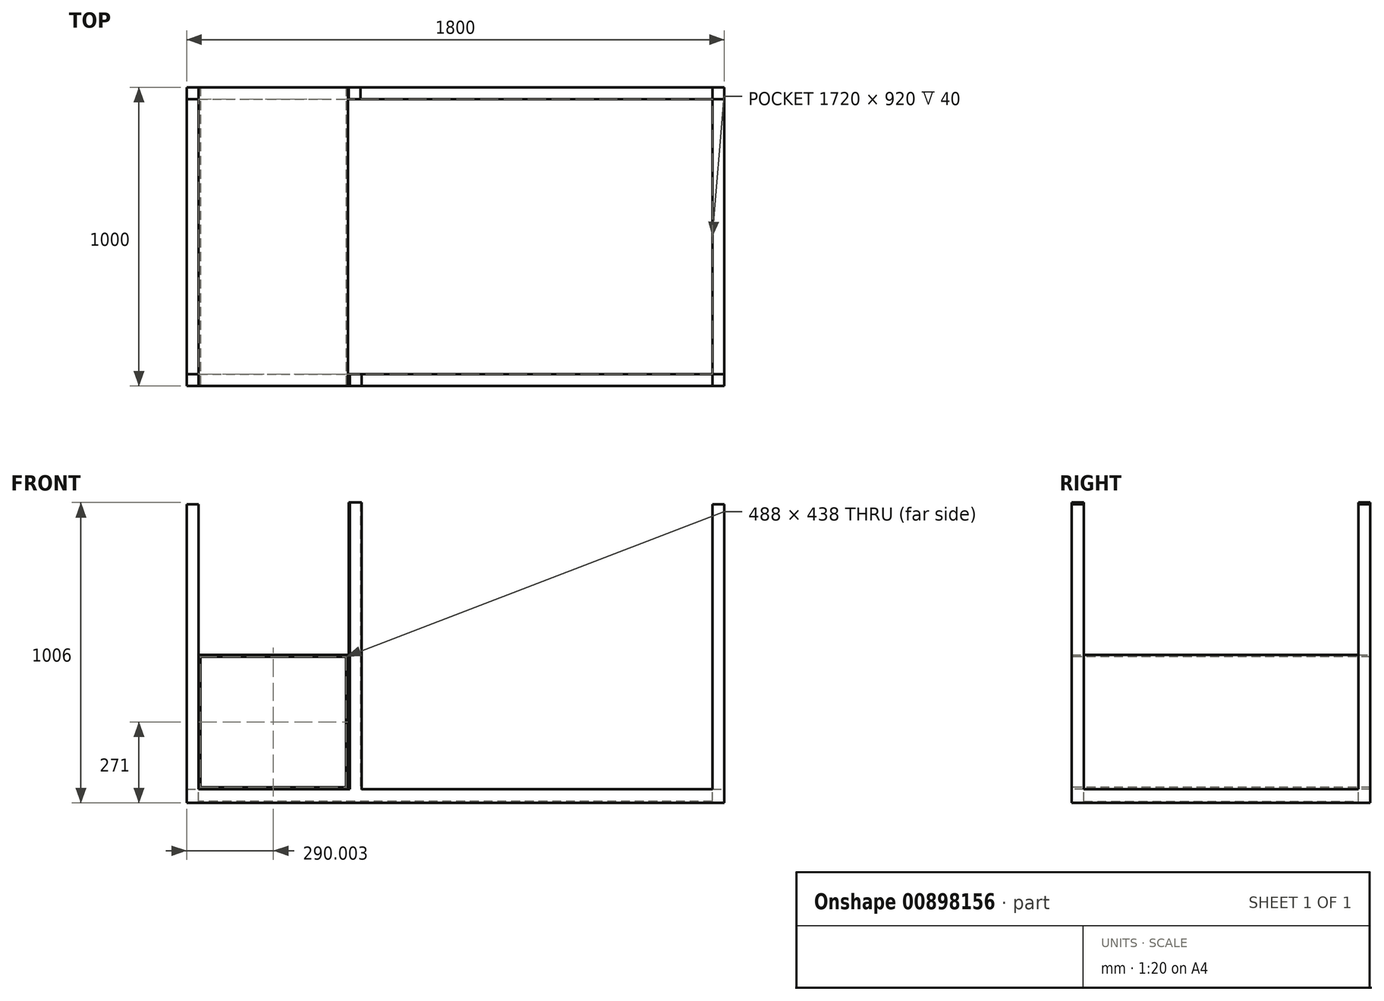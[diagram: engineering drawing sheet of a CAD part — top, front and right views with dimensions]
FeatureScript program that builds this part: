
annotation { "Feature Type Name" : "Feature", "Feature Type Description" : "" }
export const myFeature = defineFeature(function(context is Context, id is Id, definition is map)
    precondition{}
    {
        {
            var Q0;
            Q0=qCreatedBy(makeId("Top.planeOp"),FACE);
            var sketch = newSketch(context, id + "F0", { "sketchPlane" : qUnion([Q0])});
            skLineSegment(sketch, "E0.bottom", {"start": v(-904.96, 573.3) * mm, "end": v(895.04, 573.3) * mm});
            skLineSegment(sketch, "E0.top", {"start": v(-904.96, -426.7) * mm, "end": v(895.04, -426.7) * mm});
            skLineSegment(sketch, "E0.left", {"start": v(-904.96, 573.3) * mm, "end": v(-904.96, -426.7) * mm});
            skLineSegment(sketch, "E0.right", {"start": v(895.04, 573.3) * mm, "end": v(895.04, -426.7) * mm});
            skSolve(sketch);
        }
        {
            var Q0;
            Q0=makeQuery(id+"F0.imprint","IMPRINT",FACE,{"disambiguationData":[TD([[makeQuery(id+"F0.imprint","IMPRINT",EDGE,{"derivedFrom":sQuery(id+"F0.wireOp",EDGE,"E0.bottom")}),-1.0]])]});
            extrude(context, id + "F1", {"entities" : qUnion([Q0]), "depth" : 6 * mm, "offsetDistance" : 25 * mm});
        }
        {
            var Q0;
            Q0=makeQuery(id+"F1.opExtrude","CAP_FACE",FACE,{"disambiguationData":[OSD([sQuery(id+"F0.wireOp",EDGE,"E0.bottom"),sQuery(id+"F0.wireOp",EDGE,"E0.top"),sQuery(id+"F0.wireOp",EDGE,"E0.left"),sQuery(id+"F0.wireOp",EDGE,"E0.right")])],"isStart":true});
            var sketch = newSketch(context, id + "F2", { "sketchPlane" : qUnion([Q0])});
            skLineSegment(sketch, "E1.bottom", {"start": v(-904.96, -573.3) * mm, "end": v(-864.96, -573.3) * mm});
            skLineSegment(sketch, "E1.top", {"start": v(-904.96, -533.3) * mm, "end": v(-864.96, -533.3) * mm});
            skLineSegment(sketch, "E1.left", {"start": v(-904.96, -573.3) * mm, "end": v(-904.96, -533.3) * mm});
            skLineSegment(sketch, "E1.right", {"start": v(-864.96, -573.3) * mm, "end": v(-864.96, -533.3) * mm});
            skLineSegment(sketch, "E2.bottom", {"start": v(895.04, -573.3) * mm, "end": v(855.04, -573.3) * mm});
            skLineSegment(sketch, "E2.top", {"start": v(895.04, -533.3) * mm, "end": v(855.04, -533.3) * mm});
            skLineSegment(sketch, "E2.left", {"start": v(895.04, -573.3) * mm, "end": v(895.04, -533.3) * mm});
            skLineSegment(sketch, "E2.right", {"start": v(855.04, -573.3) * mm, "end": v(855.04, -533.3) * mm});
            skLineSegment(sketch, "E3.bottom", {"start": v(895.04, 426.7) * mm, "end": v(855.04, 426.7) * mm});
            skLineSegment(sketch, "E3.top", {"start": v(895.04, 386.7) * mm, "end": v(855.04, 386.7) * mm});
            skLineSegment(sketch, "E3.left", {"start": v(895.04, 426.7) * mm, "end": v(895.04, 386.7) * mm});
            skLineSegment(sketch, "E3.right", {"start": v(855.04, 426.7) * mm, "end": v(855.04, 386.7) * mm});
            skLineSegment(sketch, "E4.bottom", {"start": v(-904.96, 426.7) * mm, "end": v(-864.96, 426.7) * mm});
            skLineSegment(sketch, "E4.top", {"start": v(-904.96, 386.7) * mm, "end": v(-864.96, 386.7) * mm});
            skLineSegment(sketch, "E4.left", {"start": v(-904.96, 426.7) * mm, "end": v(-904.96, 386.7) * mm});
            skLineSegment(sketch, "E4.right", {"start": v(-864.96, 426.7) * mm, "end": v(-864.96, 386.7) * mm});
            skSolve(sketch);
        }
        {
            var Q0;
            Q0=makeQuery(id+"F2.imprint","IMPRINT",FACE,{"disambiguationData":[TD([[makeQuery(id+"F2.imprint","IMPRINT",EDGE,{"derivedFrom":sQuery(id+"F2.wireOp",EDGE,"E4.bottom")}),-1.0]])]});
            var Q1;
            Q1=makeQuery(id+"F2.imprint","IMPRINT",FACE,{"disambiguationData":[TD([[makeQuery(id+"F2.imprint","IMPRINT",EDGE,{"derivedFrom":sQuery(id+"F2.wireOp",EDGE,"E3.bottom")}),-1.0]])]});
            var Q2;
            Q2=makeQuery(id+"F2.imprint","IMPRINT",FACE,{"disambiguationData":[TD([[makeQuery(id+"F2.imprint","IMPRINT",EDGE,{"derivedFrom":sQuery(id+"F2.wireOp",EDGE,"E2.bottom")}),1.0]])]});
            var Q3;
            Q3=makeQuery(id+"F2.imprint","IMPRINT",FACE,{"disambiguationData":[TD([[makeQuery(id+"F2.imprint","IMPRINT",EDGE,{"derivedFrom":sQuery(id+"F2.wireOp",EDGE,"E1.bottom")}),1.0]])]});
            extrude(context, id + "F3", {"entities" : qUnion([Q0, Q1, Q2, Q3]), "operationType" : NewBodyOperationType.ADD, "depth" : -1000 * mm, "offsetDistance" : 25 * mm});
        }
        {
            var Q0;
            Q0=makeQuery(id+"F3.opExtrude","SWEPT_FACE",FACE,{"disambiguationData":[OSD([sQuery(id+"F2.wireOp",EDGE,"E3.top")])]});
            var sketch = newSketch(context, id + "F4", { "sketchPlane" : qUnion([Q0])});
            skLineSegment(sketch, "E5.bottom", {"start": v(-855.04, 6) * mm, "end": v(-895.04, 6) * mm});
            skLineSegment(sketch, "E5.top", {"start": v(-855.04, 46) * mm, "end": v(-895.04, 46) * mm});
            skLineSegment(sketch, "E5.left", {"start": v(-855.04, 6) * mm, "end": v(-855.04, 46) * mm});
            skLineSegment(sketch, "E5.right", {"start": v(-895.04, 6) * mm, "end": v(-895.04, 46) * mm});
            skSolve(sketch);
        }
        {
            var Q0;
            Q0=makeQuery(id+"F4.imprint","IMPRINT",FACE,{"disambiguationData":[TD([[makeQuery(id+"F4.imprint","IMPRINT",EDGE,{"derivedFrom":sQuery(id+"F4.wireOp",EDGE,"E5.bottom")}),-1.0]])]});
            extrude(context, id + "F5", {"entities" : qUnion([Q0]), "operationType" : NewBodyOperationType.ADD, "depth" : 935 * mm, "offsetDistance" : 25 * mm});
        }
        {
            var Q0;
            Q0=makeQuery(id+"F5.boolean.opBoolean","MERGE",FACE,{"derivedFrom":[makeQuery(id+"F3.opExtrude","SWEPT_FACE",FACE,{"disambiguationData":[OSD([sQuery(id+"F2.wireOp",EDGE,"E2.right")])]}),makeQuery(id+"F3.opExtrude","SWEPT_FACE",FACE,{"disambiguationData":[OSD([sQuery(id+"F2.wireOp",EDGE,"E3.right")])]}),makeQuery(id+"F5.opExtrude","SWEPT_FACE",FACE,{"disambiguationData":[OSD([sQuery(id+"F4.wireOp",EDGE,"E5.left")])]})]});
            var sketch = newSketch(context, id + "F6", { "sketchPlane" : qUnion([Q0])});
            skLineSegment(sketch, "E6.bottom", {"start": v(-573.3, 6) * mm, "end": v(-533.3, 6) * mm});
            skLineSegment(sketch, "E6.top", {"start": v(-573.3, 46) * mm, "end": v(-533.3, 46) * mm});
            skLineSegment(sketch, "E6.left", {"start": v(-573.3, 6) * mm, "end": v(-573.3, 46) * mm});
            skLineSegment(sketch, "E6.right", {"start": v(-533.3, 6) * mm, "end": v(-533.3, 46) * mm});
            skSolve(sketch);
        }
        {
            var Q0;
            Q0=makeQuery(id+"F6.imprint","IMPRINT",FACE,{"disambiguationData":[TD([[makeQuery(id+"F6.imprint","IMPRINT",EDGE,{"derivedFrom":sQuery(id+"F6.wireOp",EDGE,"E6.bottom")}),-1.0]])]});
            extrude(context, id + "F7", {"entities" : qUnion([Q0]), "operationType" : NewBodyOperationType.ADD, "depth" : 1742 * mm, "offsetDistance" : 25 * mm});
        }
        {
            var Q0;
            {var subQ0=sQuery(id+"F2.wireOp",EDGE,"E3.right");var subQ1=makeQuery(id+"F3.opExtrude","SWEPT_FACE",FACE,{"disambiguationData":[OSD([subQ0])]});var subQ2=makeQuery(id+"F5.opExtrude","SWEPT_FACE",FACE,{"disambiguationData":[OSD([sQuery(id+"F4.wireOp",EDGE,"E5.left")])]});var subQ4=makeQuery(id+"F3.opExtrude","SWEPT_FACE",FACE,{"disambiguationData":[OSD([sQuery(id+"F2.wireOp",EDGE,"E2.right")])]});var subQ6=sQuery(id+"F0.wireOp",EDGE,"E0.top");Q0=makeQuery(id+"F7.boolean.opBoolean","SPLIT",FACE,{"disambiguationData":[TD([makeQuery(id+"F1.opExtrude","SWEPT_FACE",FACE,{"disambiguationData":[OSD([subQ6])]})])],"derivedFrom":makeQuery(id+"F5.boolean.opBoolean","MERGE",FACE,{"derivedFrom":[subQ4,subQ1,subQ2]})});}
            var sketch = newSketch(context, id + "F8", { "sketchPlane" : qUnion([Q0])});
            skLineSegment(sketch, "E7.bottom", {"start": v(386.7, 46) * mm, "end": v(426.7, 46) * mm});
            skLineSegment(sketch, "E7.top", {"start": v(386.7, 6) * mm, "end": v(426.7, 6) * mm});
            skLineSegment(sketch, "E7.left", {"start": v(386.7, 46) * mm, "end": v(386.7, 6) * mm});
            skLineSegment(sketch, "E7.right", {"start": v(426.7, 46) * mm, "end": v(426.7, 6) * mm});
            skSolve(sketch);
        }
        {
            var Q0;
            Q0=makeQuery(id+"F8.imprint","IMPRINT",FACE,{"disambiguationData":[TD([[makeQuery(id+"F8.imprint","IMPRINT",EDGE,{"derivedFrom":sQuery(id+"F8.wireOp",EDGE,"E7.bottom")}),-1.0]])]});
            extrude(context, id + "F9", {"entities" : qUnion([Q0]), "operationType" : NewBodyOperationType.ADD, "depth" : 1734 * mm, "offsetDistance" : 25 * mm});
        }
        {
            var Q0;
            Q0=makeQuery(id+"F7.boolean.opBoolean","MERGE",FACE,{"derivedFrom":[makeQuery(id+"F3.opExtrude","SWEPT_FACE",FACE,{"disambiguationData":[OSD([sQuery(id+"F2.wireOp",EDGE,"E1.top")])]}),makeQuery(id+"F7.opExtrude","SWEPT_FACE",FACE,{"disambiguationData":[OSD([sQuery(id+"F6.wireOp",EDGE,"E6.right")])]})]});
            var sketch = newSketch(context, id + "F10", { "sketchPlane" : qUnion([Q0])});
            skLineSegment(sketch, "E8.bottom", {"start": v(-904.96, 6) * mm, "end": v(-864.96, 6) * mm});
            skLineSegment(sketch, "E8.top", {"start": v(-904.96, 46) * mm, "end": v(-864.96, 46) * mm});
            skLineSegment(sketch, "E8.left", {"start": v(-904.96, 6) * mm, "end": v(-904.96, 46) * mm});
            skLineSegment(sketch, "E8.right", {"start": v(-864.96, 6) * mm, "end": v(-864.96, 46) * mm});
            skSolve(sketch);
        }
        {
            var Q0;
            Q0 = qSketchRegion(id + "F10", true);
            extrude(context, id + "F11", {"entities" : qUnion([Q0]), "operationType" : NewBodyOperationType.ADD, "depth" : 941 * mm, "offsetDistance" : 25 * mm});
        }
        {
            var Q0;
            Q0=makeQuery(id+"F9.boolean.opBoolean","MERGE",FACE,{"derivedFrom":[makeQuery(id+"F3.boolean.opBoolean","MERGE",FACE,{"derivedFrom":[makeQuery(id+"F1.opExtrude","SWEPT_FACE",FACE,{"disambiguationData":[OSD([sQuery(id+"F0.wireOp",EDGE,"E0.top")])]}),makeQuery(id+"F3.opExtrude","SWEPT_FACE",FACE,{"disambiguationData":[OSD([sQuery(id+"F2.wireOp",EDGE,"E3.bottom")])]}),makeQuery(id+"F3.opExtrude","SWEPT_FACE",FACE,{"disambiguationData":[OSD([sQuery(id+"F2.wireOp",EDGE,"E4.bottom")])]})]}),makeQuery(id+"F9.opExtrude","SWEPT_FACE",FACE,{"disambiguationData":[OSD([sQuery(id+"F8.wireOp",EDGE,"E7.right")])]})]});
            var sketch = newSketch(context, id + "F12", { "sketchPlane" : qUnion([Q0])});
            skLineSegment(sketch, "E9.bottom", {"start": v(-864.96, 46) * mm, "end": v(-364.96, 46) * mm});
            skLineSegment(sketch, "E9.top", {"start": v(-864.96, 496) * mm, "end": v(-364.96, 496) * mm});
            skLineSegment(sketch, "E9.left", {"start": v(-864.96, 46) * mm, "end": v(-864.96, 496) * mm});
            skLineSegment(sketch, "E9.right", {"start": v(-364.96, 46) * mm, "end": v(-364.96, 496) * mm});
            skSolve(sketch);
        }
        {
            var Q0;
            Q0=makeQuery(id+"F12.imprint","IMPRINT",FACE,{"disambiguationData":[TD([[makeQuery(id+"F12.imprint","IMPRINT",EDGE,{"derivedFrom":sQuery(id+"F12.wireOp",EDGE,"E9.bottom")}),1.0]])]});
            extrude(context, id + "F13", {"entities" : qUnion([Q0]), "oppositeDirection" : true, "depth" : 1000 * mm, "offsetDistance" : 25 * mm, "hasDraft" : true, "draftAngle" : 0 * degree});
        }
        {
            var Q0;
            Q0=makeQuery(id+"F13.opExtrude","CAP_FACE",FACE,{"disambiguationData":[OSD([sQuery(id+"F12.wireOp",EDGE,"E9.bottom"),sQuery(id+"F12.wireOp",EDGE,"E9.top"),sQuery(id+"F12.wireOp",EDGE,"E9.left"),sQuery(id+"F12.wireOp",EDGE,"E9.right")])],"isStart":true});
            var sketch = newSketch(context, id + "F14", { "sketchPlane" : qUnion([Q0])});
            skLineSegment(sketch, "E10.bottom", {"start": v(-370.96, 52) * mm, "end": v(-858.96, 52) * mm});
            skLineSegment(sketch, "E10.top", {"start": v(-370.96, 490) * mm, "end": v(-858.96, 490) * mm});
            skLineSegment(sketch, "E10.left", {"start": v(-370.96, 52) * mm, "end": v(-370.96, 490) * mm});
            skLineSegment(sketch, "E10.right", {"start": v(-858.96, 52) * mm, "end": v(-858.96, 490) * mm});
            skSolve(sketch);
        }
        {
            var Q0;
            Q0=makeQuery(id+"F14.imprint","IMPRINT",FACE,{"disambiguationData":[TD([[makeQuery(id+"F14.imprint","IMPRINT",EDGE,{"derivedFrom":sQuery(id+"F14.wireOp",EDGE,"E10.bottom")}),-1.0]])]});
            extrude(context, id + "F15", {"entities" : qUnion([Q0]), "operationType" : NewBodyOperationType.REMOVE, "oppositeDirection" : true, "depth" : 1308 * mm, "offsetDistance" : 25 * mm});
        }
        {
            var Q0;
            Q0=makeQuery(id+"F9.opExtrude","SWEPT_FACE",FACE,{"disambiguationData":[OSD([sQuery(id+"F8.wireOp",EDGE,"E7.bottom")])]});
            var sketch = newSketch(context, id + "F16", { "sketchPlane" : qUnion([Q0])});
            skLineSegment(sketch, "E11.bottom", {"start": v(-359.05, -386.7) * mm, "end": v(-319.05, -386.7) * mm});
            skLineSegment(sketch, "E11.top", {"start": v(-359.05, -426.7) * mm, "end": v(-319.05, -426.7) * mm});
            skLineSegment(sketch, "E11.left", {"start": v(-359.05, -386.7) * mm, "end": v(-359.05, -426.7) * mm});
            skLineSegment(sketch, "E11.right", {"start": v(-319.05, -386.7) * mm, "end": v(-319.05, -426.7) * mm});
            skSolve(sketch);
        }
        {
            var Q0;
            Q0=makeQuery(id+"F7.opExtrude","SWEPT_FACE",FACE,{"disambiguationData":[OSD([sQuery(id+"F6.wireOp",EDGE,"E6.top")])]});
            var sketch = newSketch(context, id + "F17", { "sketchPlane" : qUnion([Q0])});
            skLineSegment(sketch, "E12.bottom", {"start": v(-362.83, 573.3) * mm, "end": v(-322.83, 573.3) * mm});
            skLineSegment(sketch, "E12.top", {"start": v(-362.83, 533.3) * mm, "end": v(-322.83, 533.3) * mm});
            skLineSegment(sketch, "E12.left", {"start": v(-362.83, 573.3) * mm, "end": v(-362.83, 533.3) * mm});
            skLineSegment(sketch, "E12.right", {"start": v(-322.83, 573.3) * mm, "end": v(-322.83, 533.3) * mm});
            skSolve(sketch);
        }
        {
            var Q0;
            Q0=makeQuery(id+"F16.imprint","IMPRINT",FACE,{"disambiguationData":[TD([[makeQuery(id+"F16.imprint","IMPRINT",EDGE,{"derivedFrom":sQuery(id+"F16.wireOp",EDGE,"E11.bottom")}),-1.0]])]});
            var Q1;
            Q1=makeQuery(id+"F17.imprint","IMPRINT",FACE,{"disambiguationData":[TD([[makeQuery(id+"F17.imprint","IMPRINT",EDGE,{"derivedFrom":sQuery(id+"F17.wireOp",EDGE,"E12.bottom")}),-1.0]])]});
            extrude(context, id + "F18", {"entities" : qUnion([Q0, Q1]), "operationType" : NewBodyOperationType.ADD, "depth" : 960 * mm, "offsetDistance" : 25 * mm});
        }
    });
